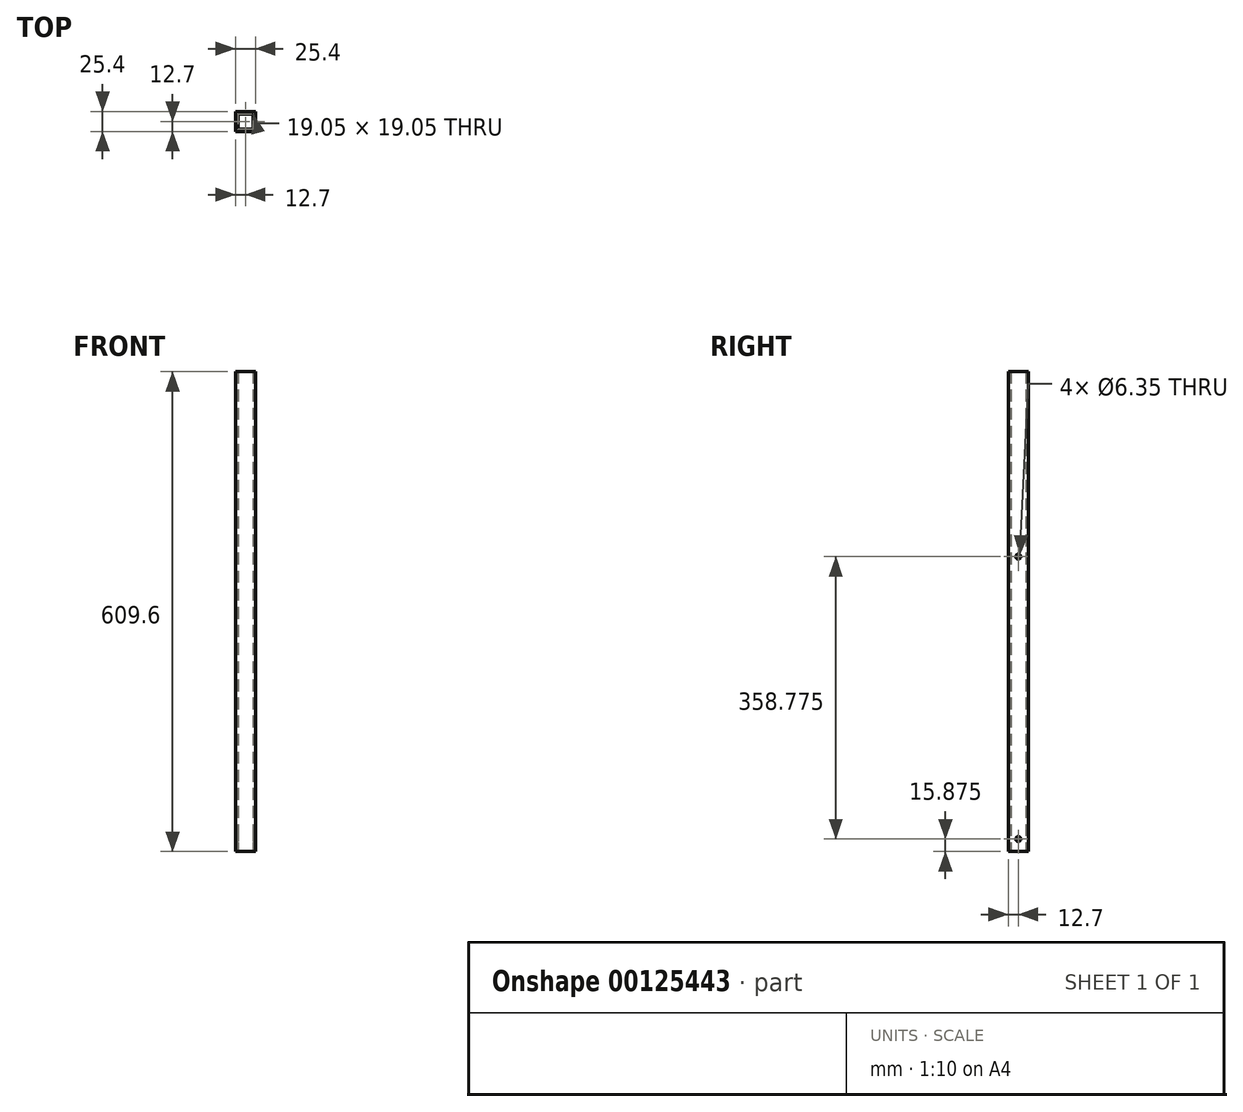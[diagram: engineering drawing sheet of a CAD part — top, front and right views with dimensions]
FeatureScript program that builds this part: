
annotation { "Feature Type Name" : "Feature", "Feature Type Description" : "" }
export const myFeature = defineFeature(function(context is Context, id is Id, definition is map)
    precondition{}
    {
        {
            var Q0;
            Q0=qCreatedBy(makeId("Top.planeOp"),FACE);
            var sketch = newSketch(context, id + "F0", { "sketchPlane" : qUnion([Q0])});
            skLineSegment(sketch, "E0.bottom", {"start": v(12.7, -12.7) * mm, "end": v(-12.7, -12.7) * mm});
            skLineSegment(sketch, "E0.top", {"start": v(12.7, 12.7) * mm, "end": v(-12.7, 12.7) * mm});
            skLineSegment(sketch, "E0.left", {"start": v(12.7, -12.7) * mm, "end": v(12.7, 12.7) * mm});
            skLineSegment(sketch, "E0.right", {"start": v(-12.7, -12.7) * mm, "end": v(-12.7, 12.7) * mm});
            skPoint(sketch, "E0.middle", {"position": v(0, 0) * mm});
            skLineSegment(sketch, "E1.bottom", {"start": v(9.53, -9.53) * mm, "end": v(-9.53, -9.53) * mm});
            skLineSegment(sketch, "E1.top", {"start": v(9.53, 9.53) * mm, "end": v(-9.53, 9.53) * mm});
            skLineSegment(sketch, "E1.left", {"start": v(9.53, -9.53) * mm, "end": v(9.53, 9.53) * mm});
            skLineSegment(sketch, "E1.right", {"start": v(-9.53, -9.52) * mm, "end": v(-9.53, 9.53) * mm});
            skSolve(sketch);
        }
        {
            var Q0;
            Q0 = qSketchRegion(id + "F0", true);
            extrude(context, id + "F1", {"entities" : qUnion([Q0]), "endBound" : BoundingType.SYMMETRIC, "depth" : 609.6 * mm});
        }
        {
            var Q0;
            Q0=makeQuery(id+"F1.opExtrude","SWEPT_FACE",FACE,{"disambiguationData":[OSD([sQuery(id+"F0.wireOp",EDGE,"E0.right")])]});
            var sketch = newSketch(context, id + "F2", { "sketchPlane" : qUnion([Q0])});
            skCircle(sketch, "E2", {"center": v(0, 69.85) * mm, "radius": 3.18 * mm});
            skCircle(sketch, "E3", {"center": v(0, -288.93) * mm, "radius": 3.18 * mm});
            skSolve(sketch);
        }
        {
            var Q0;
            Q0 = qSketchRegion(id + "F2", true);
            extrude(context, id + "F3", {"entities" : qUnion([Q0]), "operationType" : NewBodyOperationType.REMOVE, "oppositeDirection" : true, "depth" : 31.75 * mm});
        }
    });
